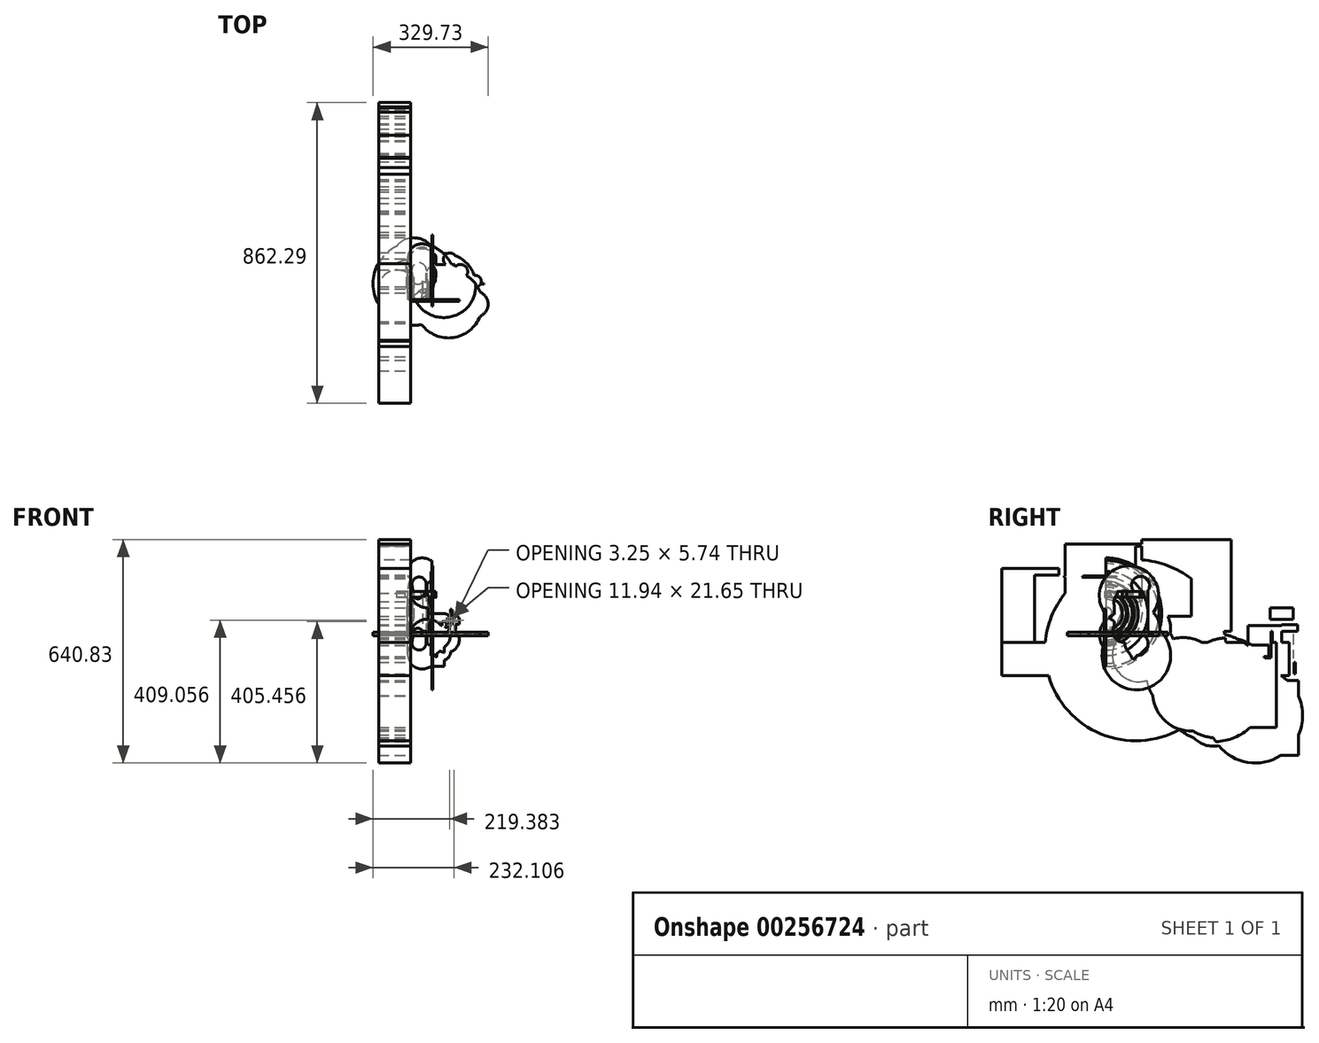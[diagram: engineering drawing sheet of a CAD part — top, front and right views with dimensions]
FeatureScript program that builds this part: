
annotation { "Feature Type Name" : "Feature", "Feature Type Description" : "" }
export const myFeature = defineFeature(function(context is Context, id is Id, definition is map)
    precondition{}
    {
        {
            var Q0;
            Q0=qCreatedBy(makeId("Top.planeOp"),FACE);
            var sketch = newSketch(context, id + "F0", { "sketchPlane" : qUnion([Q0])});
            skCircle(sketch, "E0", {"center": v(3, 0) * mm, "radius": 59.26 * mm});
            skCircle(sketch, "E1", {"center": v(60.76, 0) * mm, "radius": 10.8 * mm});
            skCircle(sketch, "E2", {"center": v(-11.73, 4.21) * mm, "radius": 51.95 * mm});
            skCircle(sketch, "E3", {"center": v(26.17, -8.72) * mm, "radius": 40 * mm});
            skCircle(sketch, "E4", {"center": v(-2.7, 22.56) * mm, "radius": 6.86 * mm});
            skCircle(sketch, "E5", {"center": v(9.93, 33.09) * mm, "radius": 17.65 * mm});
            skCircle(sketch, "E6", {"center": v(29.48, 15.94) * mm, "radius": 43.32 * mm});
            skCircle(sketch, "E7", {"center": v(-30.68, -24.97) * mm, "radius": 24.63 * mm});
            skCircle(sketch, "E8", {"center": v(16.24, 43.01) * mm, "radius": 6.92 * mm});
            skLineSegment(sketch, "E9.bottom", {"start": v(-9.54, 34.78) * mm, "end": v(37.9, 34.78) * mm});
            skLineSegment(sketch, "E9.top", {"start": v(-9.54, 34.9) * mm, "end": v(37.9, 34.9) * mm});
            skLineSegment(sketch, "E9.left", {"start": v(-9.54, 34.78) * mm, "end": v(-9.54, 34.9) * mm});
            skLineSegment(sketch, "E9.right", {"start": v(37.9, 34.78) * mm, "end": v(37.9, 34.9) * mm});
            skLineSegment(sketch, "E10.bottom", {"start": v(-6.92, -8.42) * mm, "end": v(-20.75, -8.42) * mm});
            skLineSegment(sketch, "E10.top", {"start": v(-6.92, -25.87) * mm, "end": v(-20.75, -25.87) * mm});
            skLineSegment(sketch, "E10.left", {"start": v(-6.92, -8.42) * mm, "end": v(-6.92, -25.87) * mm});
            skLineSegment(sketch, "E10.right", {"start": v(-20.75, -8.42) * mm, "end": v(-20.75, -25.87) * mm});
            skLineSegment(sketch, "E11.bottom", {"start": v(-21.06, -25.87) * mm, "end": v(-3.3, -25.87) * mm});
            skLineSegment(sketch, "E11.top", {"start": v(-21.06, -8.12) * mm, "end": v(-3.3, -8.12) * mm});
            skLineSegment(sketch, "E11.left", {"start": v(-21.06, -25.87) * mm, "end": v(-21.06, -8.12) * mm});
            skLineSegment(sketch, "E11.right", {"start": v(-3.3, -25.87) * mm, "end": v(-3.3, -8.12) * mm});
            skLineSegment(sketch, "E12.bottom", {"start": v(6.32, 9.93) * mm, "end": v(6.92, 9.93) * mm});
            skLineSegment(sketch, "E12.top", {"start": v(6.32, 15.64) * mm, "end": v(6.92, 15.64) * mm});
            skLineSegment(sketch, "E12.left", {"start": v(6.32, 9.93) * mm, "end": v(6.32, 15.64) * mm});
            skLineSegment(sketch, "E12.right", {"start": v(6.92, 9.93) * mm, "end": v(6.92, 15.64) * mm});
            skLineSegment(sketch, "E13.bottom", {"start": v(-0.9, -17.75) * mm, "end": v(-3, -17.75) * mm});
            skLineSegment(sketch, "E13.top", {"start": v(-0.9, -37.3) * mm, "end": v(-3, -37.3) * mm});
            skLineSegment(sketch, "E13.left", {"start": v(-0.9, -17.75) * mm, "end": v(-0.9, -37.3) * mm});
            skLineSegment(sketch, "E13.right", {"start": v(-3, -17.75) * mm, "end": v(-3, -37.3) * mm});
            skLineSegment(sketch, "E14.bottom", {"start": v(-0.9, -37.3) * mm, "end": v(18.05, -37.3) * mm});
            skLineSegment(sketch, "E14.top", {"start": v(-0.9, -31.58) * mm, "end": v(18.05, -31.58) * mm});
            skLineSegment(sketch, "E14.left", {"start": v(-0.9, -37.3) * mm, "end": v(-0.9, -31.58) * mm});
            skLineSegment(sketch, "E14.right", {"start": v(18.05, -37.3) * mm, "end": v(18.05, -31.58) * mm});
            skLineSegment(sketch, "E15.bottom", {"start": v(23.46, -22.56) * mm, "end": v(18.05, -22.56) * mm});
            skLineSegment(sketch, "E15.top", {"start": v(23.46, -1.5) * mm, "end": v(18.05, -1.5) * mm});
            skLineSegment(sketch, "E15.left", {"start": v(23.46, -22.56) * mm, "end": v(23.46, -1.5) * mm});
            skLineSegment(sketch, "E15.right", {"start": v(18.05, -22.56) * mm, "end": v(18.05, -1.5) * mm});
            skLineSegment(sketch, "E16.bottom", {"start": v(16.84, -0.3) * mm, "end": v(63.77, -0.3) * mm});
            skLineSegment(sketch, "E16.top", {"start": v(16.84, 50.23) * mm, "end": v(63.77, 50.23) * mm});
            skLineSegment(sketch, "E16.left", {"start": v(16.84, -0.3) * mm, "end": v(16.84, 50.23) * mm});
            skLineSegment(sketch, "E16.right", {"start": v(63.77, -0.3) * mm, "end": v(63.77, 50.23) * mm});
            skLineSegment(sketch, "E17.bottom", {"start": v(35.14, -27) * mm, "end": v(-31.88, -27) * mm});
            skLineSegment(sketch, "E17.top", {"start": v(35.14, 42.71) * mm, "end": v(-31.88, 42.71) * mm});
            skLineSegment(sketch, "E17.left", {"start": v(35.14, -27) * mm, "end": v(35.14, 42.71) * mm});
            skLineSegment(sketch, "E17.right", {"start": v(-31.88, -27) * mm, "end": v(-31.88, 42.71) * mm});
            skSolve(sketch);
        }
        {
            var Q0;
            Q0 = qSketchRegion(id + "F0", true);
            extrude(context, id + "F1", {"entities" : qUnion([Q0]), "depth" : 17.53 * mm});
        }
        {
            var Q0;
            {var subQ0=sQuery(id+"F0.wireOp",EDGE,"E16.right");Q0=makeQuery(id+"F1.opExtrude","SWEPT_FACE",FACE,{"disambiguationData":[OSD([subQ0]),TDD([makeQuery(id+"F0.imprint","IMPRINT",EDGE,{"disambiguationData":[TD([[makeQuery(id+"F0.imprint","INTERSECT",VERTEX,{"derivedFrom":[sQuery(id+"F0.wireOp",EDGE,"E1"),subQ0]}),1.0]])],"derivedFrom":subQ0})])]});}
            var sketch = newSketch(context, id + "F2", { "sketchPlane" : qUnion([Q0])});
            skCircle(sketch, "E18", {"center": v(-10.37, 5.14) * mm, "radius": 85.17 * mm});
            skCircle(sketch, "E19", {"center": v(-43.61, 34.5) * mm, "radius": 25.84 * mm});
            skCircle(sketch, "E20", {"center": v(-26.77, -16.98) * mm, "radius": 29.62 * mm});
            skCircle(sketch, "E21", {"center": v(0.3, -14.85) * mm, "radius": 32.69 * mm});
            skCircle(sketch, "E22", {"center": v(3.91, -97.37) * mm, "radius": 31.8 * mm});
            skCircle(sketch, "E23", {"center": v(-25.27, -65.04) * mm, "radius": 7.85 * mm});
            skCircle(sketch, "E24", {"center": v(-34.3, -47.6) * mm, "radius": 19.67 * mm});
            skCircle(sketch, "E25", {"center": v(-24.06, -169.26) * mm, "radius": 7.04 * mm});
            skCircle(sketch, "E26", {"center": v(-32.79, -122.47) * mm, "radius": 16.44 * mm});
            skCircle(sketch, "E27", {"center": v(-41.8, -88.01) * mm, "radius": 57.72 * mm});
            skCircle(sketch, "E28", {"center": v(11.43, -107.58) * mm, "radius": 62.26 * mm});
            skCircle(sketch, "E29", {"center": v(-19.55, -161.18) * mm, "radius": 6.63 * mm});
            skCircle(sketch, "E30", {"center": v(-32.18, -133.53) * mm, "radius": 33.19 * mm});
            skCircle(sketch, "E31", {"center": v(-31.58, -166.7) * mm, "radius": 98.41 * mm});
            skLineSegment(sketch, "E32.bottom", {"start": v(0, -65.82) * mm, "end": v(12.03, -65.82) * mm});
            skLineSegment(sketch, "E32.top", {"start": v(0, -38.67) * mm, "end": v(12.03, -38.67) * mm});
            skLineSegment(sketch, "E32.left", {"start": v(0, -65.82) * mm, "end": v(0, -38.67) * mm});
            skLineSegment(sketch, "E32.right", {"start": v(12.03, -65.82) * mm, "end": v(12.03, -38.67) * mm});
            skLineSegment(sketch, "E33.bottom", {"start": v(18.05, -31.86) * mm, "end": v(-13.18, -31.86) * mm});
            skLineSegment(sketch, "E33.top", {"start": v(18.05, -124.18) * mm, "end": v(-13.18, -124.18) * mm});
            skLineSegment(sketch, "E33.left", {"start": v(18.05, -31.86) * mm, "end": v(18.05, -124.18) * mm});
            skLineSegment(sketch, "E33.right", {"start": v(-13.18, -31.86) * mm, "end": v(-13.18, -124.18) * mm});
            skLineSegment(sketch, "E34.bottom", {"start": v(-8.12, -118.22) * mm, "end": v(-37.9, -118.22) * mm});
            skLineSegment(sketch, "E34.top", {"start": v(-8.12, -5.92) * mm, "end": v(-37.9, -5.92) * mm});
            skLineSegment(sketch, "E34.left", {"start": v(-8.12, -118.22) * mm, "end": v(-8.12, -5.92) * mm});
            skLineSegment(sketch, "E34.right", {"start": v(-37.9, -118.22) * mm, "end": v(-37.9, -5.92) * mm});
            skLineSegment(sketch, "E35.bottom", {"start": v(32.3, -8.23) * mm, "end": v(-46.92, -8.23) * mm});
            skLineSegment(sketch, "E35.top", {"start": v(32.3, -108.86) * mm, "end": v(-46.92, -108.86) * mm});
            skLineSegment(sketch, "E35.left", {"start": v(32.3, -8.23) * mm, "end": v(32.3, -108.86) * mm});
            skLineSegment(sketch, "E35.right", {"start": v(-46.92, -8.23) * mm, "end": v(-46.92, -108.86) * mm});
            skLineSegment(sketch, "E36.bottom", {"start": v(-64.67, -110.13) * mm, "end": v(61.36, -110.13) * mm});
            skLineSegment(sketch, "E36.top", {"start": v(-64.67, 41.3) * mm, "end": v(61.36, 41.3) * mm});
            skLineSegment(sketch, "E36.left", {"start": v(-64.67, -110.13) * mm, "end": v(-64.67, 41.3) * mm});
            skLineSegment(sketch, "E36.right", {"start": v(61.36, -110.13) * mm, "end": v(61.36, 41.3) * mm});
            skSolve(sketch);
        }
        {
            var Q0;
            Q0 = qSketchRegion(id + "F2", true);
            extrude(context, id + "F3", {"entities" : qUnion([Q0]), "operationType" : NewBodyOperationType.ADD, "depth" : 2.54 * mm});
        }
        {
            var Q0;
            {var subQ0=sQuery(id+"F2.wireOp",EDGE,"E36.bottom");Q0=makeQuery(id+"F3.opExtrude","SWEPT_FACE",FACE,{"disambiguationData":[OSD([subQ0]),TDD([makeQuery(id+"F2.imprint","IMPRINT",EDGE,{"disambiguationData":[TD([[makeQuery(id+"F2.imprint","INTERSECT",VERTEX,{"derivedFrom":[subQ0,sQuery(id+"F2.wireOp",EDGE,"E36.left")]}),-1.0]])],"derivedFrom":subQ0})])]});}
            var sketch = newSketch(context, id + "F4", { "sketchPlane" : qUnion([Q0])});
            skLineSegment(sketch, "E37.bottom", {"start": v(32.71, 16.54) * mm, "end": v(45.9, 16.54) * mm});
            skLineSegment(sketch, "E37.top", {"start": v(32.71, 11.73) * mm, "end": v(45.9, 11.73) * mm});
            skLineSegment(sketch, "E37.left", {"start": v(32.71, 16.54) * mm, "end": v(32.71, 11.73) * mm});
            skLineSegment(sketch, "E37.right", {"start": v(45.9, 16.54) * mm, "end": v(45.9, 11.73) * mm});
            skLineSegment(sketch, "E38.bottom", {"start": v(97.8, -17.45) * mm, "end": v(125.87, -17.45) * mm});
            skLineSegment(sketch, "E38.top", {"start": v(97.8, -33.39) * mm, "end": v(125.87, -33.39) * mm});
            skLineSegment(sketch, "E38.left", {"start": v(97.8, -17.45) * mm, "end": v(97.8, -33.39) * mm});
            skLineSegment(sketch, "E38.right", {"start": v(125.87, -17.45) * mm, "end": v(125.87, -33.39) * mm});
            skLineSegment(sketch, "E39.bottom", {"start": v(127.57, -33.39) * mm, "end": v(4.64, -33.39) * mm});
            skLineSegment(sketch, "E39.top", {"start": v(127.57, 44.52) * mm, "end": v(4.64, 44.52) * mm});
            skLineSegment(sketch, "E39.left", {"start": v(127.57, -33.39) * mm, "end": v(127.57, 44.52) * mm});
            skLineSegment(sketch, "E39.right", {"start": v(4.64, -33.39) * mm, "end": v(4.64, 44.52) * mm});
            skLineSegment(sketch, "E40.bottom", {"start": v(4.64, 44.52) * mm, "end": v(125.87, 44.52) * mm});
            skLineSegment(sketch, "E40.top", {"start": v(4.64, -21.06) * mm, "end": v(125.87, -21.06) * mm});
            skLineSegment(sketch, "E40.left", {"start": v(4.64, 44.52) * mm, "end": v(4.64, -21.06) * mm});
            skLineSegment(sketch, "E40.right", {"start": v(125.87, 44.52) * mm, "end": v(125.87, -21.06) * mm});
            skLineSegment(sketch, "E41.bottom", {"start": v(199.04, -10.83) * mm, "end": v(211.37, -10.83) * mm});
            skLineSegment(sketch, "E41.top", {"start": v(199.04, -9.93) * mm, "end": v(211.37, -9.93) * mm});
            skLineSegment(sketch, "E41.left", {"start": v(199.04, -10.83) * mm, "end": v(199.04, -9.93) * mm});
            skLineSegment(sketch, "E41.right", {"start": v(211.37, -10.83) * mm, "end": v(211.37, -9.93) * mm});
            skLineSegment(sketch, "E42.bottom", {"start": v(213.08, -9.93) * mm, "end": v(61.22, -9.93) * mm});
            skLineSegment(sketch, "E42.top", {"start": v(213.08, -9.93) * mm, "end": v(61.22, -9.93) * mm});
            skLineSegment(sketch, "E42.left", {"start": v(213.08, -9.93) * mm, "end": v(213.08, -9.93) * mm});
            skLineSegment(sketch, "E42.right", {"start": v(61.22, -9.93) * mm, "end": v(61.22, -9.93) * mm});
            skLineSegment(sketch, "E43.bottom", {"start": v(61.22, -8.72) * mm, "end": v(68.02, -8.72) * mm});
            skLineSegment(sketch, "E43.top", {"start": v(61.22, 2.7) * mm, "end": v(68.02, 2.7) * mm});
            skLineSegment(sketch, "E43.left", {"start": v(61.22, -8.72) * mm, "end": v(61.22, 2.7) * mm});
            skLineSegment(sketch, "E43.right", {"start": v(68.02, -8.72) * mm, "end": v(68.02, 2.7) * mm});
            skLineSegment(sketch, "E44.bottom", {"start": v(92.7, 24.97) * mm, "end": v(112.26, 24.97) * mm});
            skLineSegment(sketch, "E44.top", {"start": v(92.7, 36.1) * mm, "end": v(112.26, 36.1) * mm});
            skLineSegment(sketch, "E44.left", {"start": v(92.7, 24.97) * mm, "end": v(92.7, 36.1) * mm});
            skLineSegment(sketch, "E44.right", {"start": v(112.26, 24.97) * mm, "end": v(112.26, 36.1) * mm});
            skLineSegment(sketch, "E45.bottom", {"start": v(123.75, 38.5) * mm, "end": v(65.04, 38.5) * mm});
            skLineSegment(sketch, "E45.top", {"start": v(123.75, -46.92) * mm, "end": v(65.04, -46.92) * mm});
            skLineSegment(sketch, "E45.left", {"start": v(123.75, 38.5) * mm, "end": v(123.75, -46.92) * mm});
            skLineSegment(sketch, "E45.right", {"start": v(65.04, 38.5) * mm, "end": v(65.04, -46.92) * mm});
            skLineSegment(sketch, "E46.bottom", {"start": v(65.04, -46.92) * mm, "end": v(7.2, -46.92) * mm});
            skLineSegment(sketch, "E46.top", {"start": v(65.04, -56.25) * mm, "end": v(7.2, -56.25) * mm});
            skLineSegment(sketch, "E46.left", {"start": v(65.04, -46.92) * mm, "end": v(65.04, -56.25) * mm});
            skLineSegment(sketch, "E46.right", {"start": v(7.2, -46.92) * mm, "end": v(7.2, -56.25) * mm});
            skLineSegment(sketch, "E47.bottom", {"start": v(-51.94, -60.46) * mm, "end": v(83.76, -60.46) * mm});
            skLineSegment(sketch, "E47.top", {"start": v(-51.94, -50.53) * mm, "end": v(83.76, -50.53) * mm});
            skLineSegment(sketch, "E47.left", {"start": v(-51.94, -60.46) * mm, "end": v(-51.94, -50.53) * mm});
            skLineSegment(sketch, "E47.right", {"start": v(83.76, -60.46) * mm, "end": v(83.76, -50.53) * mm});
            skLineSegment(sketch, "E48.bottom", {"start": v(113.11, -52.04) * mm, "end": v(126.3, -52.04) * mm});
            skLineSegment(sketch, "E48.top", {"start": v(113.11, -53.54) * mm, "end": v(126.3, -53.54) * mm});
            skLineSegment(sketch, "E48.left", {"start": v(113.11, -52.04) * mm, "end": v(113.11, -53.54) * mm});
            skLineSegment(sketch, "E48.right", {"start": v(126.3, -52.04) * mm, "end": v(126.3, -53.54) * mm});
            skLineSegment(sketch, "E49.bottom", {"start": v(140.76, -44.22) * mm, "end": v(153.52, -44.22) * mm});
            skLineSegment(sketch, "E49.top", {"start": v(140.76, -36.7) * mm, "end": v(153.52, -36.7) * mm});
            skLineSegment(sketch, "E49.left", {"start": v(140.76, -44.22) * mm, "end": v(140.76, -36.7) * mm});
            skLineSegment(sketch, "E49.right", {"start": v(153.52, -44.22) * mm, "end": v(153.52, -36.7) * mm});
            skLineSegment(sketch, "E50.bottom", {"start": v(130.98, -11.43) * mm, "end": v(102.9, -11.43) * mm});
            skLineSegment(sketch, "E50.top", {"start": v(130.98, -6.02) * mm, "end": v(102.9, -6.02) * mm});
            skLineSegment(sketch, "E50.left", {"start": v(130.98, -11.43) * mm, "end": v(130.98, -6.02) * mm});
            skLineSegment(sketch, "E50.right", {"start": v(102.9, -11.43) * mm, "end": v(102.9, -6.02) * mm});
            skLineSegment(sketch, "E51.bottom", {"start": v(28.04, -4.51) * mm, "end": v(-6.42, -4.51) * mm});
            skLineSegment(sketch, "E51.top", {"start": v(28.04, -0.6) * mm, "end": v(-6.42, -0.6) * mm});
            skLineSegment(sketch, "E51.left", {"start": v(28.04, -4.51) * mm, "end": v(28.04, -0.6) * mm});
            skLineSegment(sketch, "E51.right", {"start": v(-6.42, -4.51) * mm, "end": v(-6.42, -0.6) * mm});
            skLineSegment(sketch, "E52.bottom", {"start": v(5.06, 20.45) * mm, "end": v(11.87, 20.45) * mm});
            skLineSegment(sketch, "E52.top", {"start": v(5.06, 24.66) * mm, "end": v(11.87, 24.66) * mm});
            skLineSegment(sketch, "E52.left", {"start": v(5.06, 20.45) * mm, "end": v(5.06, 24.66) * mm});
            skLineSegment(sketch, "E52.right", {"start": v(11.87, 20.45) * mm, "end": v(11.87, 24.66) * mm});
            skLineSegment(sketch, "E53.bottom", {"start": v(31.44, 30.08) * mm, "end": v(84.61, 30.08) * mm});
            skLineSegment(sketch, "E53.top", {"start": v(31.44, 37.9) * mm, "end": v(84.61, 37.9) * mm});
            skLineSegment(sketch, "E53.left", {"start": v(31.44, 30.08) * mm, "end": v(31.44, 37.9) * mm});
            skLineSegment(sketch, "E53.right", {"start": v(84.61, 30.08) * mm, "end": v(84.61, 37.9) * mm});
            skLineSegment(sketch, "E54.bottom", {"start": v(111.4, 28.88) * mm, "end": v(118.22, 28.88) * mm});
            skLineSegment(sketch, "E54.top", {"start": v(111.4, -59.26) * mm, "end": v(118.22, -59.26) * mm});
            skLineSegment(sketch, "E54.left", {"start": v(111.4, 28.88) * mm, "end": v(111.4, -59.26) * mm});
            skLineSegment(sketch, "E54.right", {"start": v(118.22, 28.88) * mm, "end": v(118.22, -59.26) * mm});
            skLineSegment(sketch, "E55.bottom", {"start": v(106.73, -64.07) * mm, "end": v(100.78, -64.07) * mm});
            skLineSegment(sketch, "E55.top", {"start": v(106.73, -65.87) * mm, "end": v(100.78, -65.87) * mm});
            skLineSegment(sketch, "E55.left", {"start": v(106.73, -64.07) * mm, "end": v(106.73, -65.87) * mm});
            skLineSegment(sketch, "E55.right", {"start": v(100.78, -64.07) * mm, "end": v(100.78, -65.87) * mm});
            skCircle(sketch, "E56", {"center": v(-17.9, 5.41) * mm, "radius": 11.2 * mm});
            skCircle(sketch, "E57", {"center": v(-6.85, 3.6) * mm, "radius": 19.8 * mm});
            skCircle(sketch, "E58", {"center": v(185, -69.18) * mm, "radius": 37.42 * mm});
            skCircle(sketch, "E59", {"center": v(128.85, -46.02) * mm, "radius": 47.67 * mm});
            skCircle(sketch, "E60", {"center": v(81.2, -43.92) * mm, "radius": 30.92 * mm});
            skCircle(sketch, "E61", {"center": v(108.86, -68.88) * mm, "radius": 96.95 * mm});
            skCircle(sketch, "E62", {"center": v(15.7, 38.8) * mm, "radius": 29.27 * mm});
            skCircle(sketch, "E63", {"center": v(9.74, 58.05) * mm, "radius": 63.19 * mm});
            skCircle(sketch, "E64", {"center": v(113.11, 58.65) * mm, "radius": 18.97 * mm});
            skCircle(sketch, "E65", {"center": v(143.31, 24.06) * mm, "radius": 20.76 * mm});
            skCircle(sketch, "E66", {"center": v(-38.75, -23.76) * mm, "radius": 52.4 * mm});
            skCircle(sketch, "E67", {"center": v(11.87, -10.23) * mm, "radius": 119.18 * mm});
            skCircle(sketch, "E68", {"center": v(133.1, -9.32) * mm, "radius": 12.68 * mm});
            skCircle(sketch, "E69", {"center": v(95.25, -15.64) * mm, "radius": 91.99 * mm});
            skCircle(sketch, "E70", {"center": v(186.28, -3.3) * mm, "radius": 16.6 * mm});
            skSolve(sketch);
        }
        {
            var Q0;
            Q0 = qSketchRegion(id + "F4", true);
            extrude(context, id + "F5", {"entities" : qUnion([Q0]), "operationType" : NewBodyOperationType.ADD, "depth" : 10.67 * mm});
        }
        {
            var Q0;
            Q0=makeQuery(id+"F5.opExtrude","SWEPT_FACE",FACE,{"disambiguationData":[OSD([sQuery(id+"F4.wireOp",EDGE,"E47.bottom")])]});
            var sketch = newSketch(context, id + "F6", { "sketchPlane" : qUnion([Q0])});
            skCircle(sketch, "E71", {"center": v(-48.59, -115.37) * mm, "radius": 52.6 * mm});
            skCircle(sketch, "E72", {"center": v(-33.23, -163.82) * mm, "radius": 41.84 * mm});
            skCircle(sketch, "E73", {"center": v(-26.98, -120.14) * mm, "radius": 21.12 * mm});
            skCircle(sketch, "E74", {"center": v(-39.9, -105.41) * mm, "radius": 8.6 * mm});
            skCircle(sketch, "E75", {"center": v(-21.12, -101.94) * mm, "radius": 13.58 * mm});
            skCircle(sketch, "E76", {"center": v(4.89, -108.69) * mm, "radius": 6.25 * mm});
            skCircle(sketch, "E77", {"center": v(-3, -121.26) * mm, "radius": 11.8 * mm});
            skCircle(sketch, "E78", {"center": v(-24.5, -130.43) * mm, "radius": 20.57 * mm});
            skCircle(sketch, "E79", {"center": v(-61.33, -124.29) * mm, "radius": 14.83 * mm});
            skCircle(sketch, "E80", {"center": v(-80.55, -112.88) * mm, "radius": 33.17 * mm});
            skCircle(sketch, "E81", {"center": v(-91.4, -84.6) * mm, "radius": 38.52 * mm});
            skCircle(sketch, "E82", {"center": v(-102.7, -121.42) * mm, "radius": 36.94 * mm});
            skCircle(sketch, "E83", {"center": v(-91.55, -156.63) * mm, "radius": 23.58 * mm});
            skLineSegment(sketch, "E84.bottom", {"start": v(-96.93, -198.17) * mm, "end": v(-58.06, -198.17) * mm});
            skLineSegment(sketch, "E84.top", {"start": v(-96.93, -88.5) * mm, "end": v(-58.06, -88.5) * mm});
            skLineSegment(sketch, "E84.left", {"start": v(-96.93, -198.17) * mm, "end": v(-96.93, -88.5) * mm});
            skLineSegment(sketch, "E84.right", {"start": v(-58.06, -198.17) * mm, "end": v(-58.06, -88.5) * mm});
            skLineSegment(sketch, "E85.bottom", {"start": v(-60.99, -90.34) * mm, "end": v(-68.2, -90.34) * mm});
            skLineSegment(sketch, "E85.top", {"start": v(-60.99, -94.57) * mm, "end": v(-68.2, -94.57) * mm});
            skLineSegment(sketch, "E85.left", {"start": v(-60.99, -90.34) * mm, "end": v(-60.99, -94.57) * mm});
            skLineSegment(sketch, "E85.right", {"start": v(-68.2, -90.34) * mm, "end": v(-68.2, -94.57) * mm});
            skLineSegment(sketch, "E86.bottom", {"start": v(-83.7, -93.49) * mm, "end": v(-112.61, -93.49) * mm});
            skLineSegment(sketch, "E86.top", {"start": v(-83.7, -86.24) * mm, "end": v(-112.61, -86.24) * mm});
            skLineSegment(sketch, "E86.left", {"start": v(-83.7, -93.49) * mm, "end": v(-83.7, -86.24) * mm});
            skLineSegment(sketch, "E86.right", {"start": v(-112.61, -93.49) * mm, "end": v(-112.61, -86.24) * mm});
            skLineSegment(sketch, "E87.bottom", {"start": v(-135.42, -72.46) * mm, "end": v(-129.16, -72.46) * mm});
            skLineSegment(sketch, "E87.top", {"start": v(-135.42, -53.45) * mm, "end": v(-129.16, -53.45) * mm});
            skLineSegment(sketch, "E87.left", {"start": v(-135.42, -72.46) * mm, "end": v(-135.42, -53.45) * mm});
            skLineSegment(sketch, "E87.right", {"start": v(-129.16, -72.46) * mm, "end": v(-129.16, -53.45) * mm});
            skLineSegment(sketch, "E88.bottom", {"start": v(-121.8, -51.19) * mm, "end": v(-114.29, -51.19) * mm});
            skLineSegment(sketch, "E88.top", {"start": v(-121.8, -53.88) * mm, "end": v(-114.29, -53.88) * mm});
            skLineSegment(sketch, "E88.left", {"start": v(-121.8, -51.19) * mm, "end": v(-121.8, -53.88) * mm});
            skLineSegment(sketch, "E88.right", {"start": v(-114.29, -51.19) * mm, "end": v(-114.29, -53.88) * mm});
            skLineSegment(sketch, "E89.bottom", {"start": v(-102.9, -68.88) * mm, "end": v(-89.86, -68.88) * mm});
            skLineSegment(sketch, "E89.top", {"start": v(-102.9, -84.33) * mm, "end": v(-89.86, -84.33) * mm});
            skLineSegment(sketch, "E89.left", {"start": v(-102.9, -68.88) * mm, "end": v(-102.9, -84.33) * mm});
            skLineSegment(sketch, "E89.right", {"start": v(-89.86, -68.88) * mm, "end": v(-89.86, -84.33) * mm});
            skLineSegment(sketch, "E90.bottom", {"start": v(-77.22, -96.36) * mm, "end": v(-62.89, -96.36) * mm});
            skLineSegment(sketch, "E90.top", {"start": v(-77.22, -102.88) * mm, "end": v(-62.89, -102.88) * mm});
            skLineSegment(sketch, "E90.left", {"start": v(-77.22, -96.36) * mm, "end": v(-77.22, -102.88) * mm});
            skLineSegment(sketch, "E90.right", {"start": v(-62.89, -96.36) * mm, "end": v(-62.89, -102.88) * mm});
            skLineSegment(sketch, "E91.bottom", {"start": v(-51.23, -106.1) * mm, "end": v(-87.55, -106.1) * mm});
            skLineSegment(sketch, "E91.top", {"start": v(-51.23, -46.27) * mm, "end": v(-87.55, -46.27) * mm});
            skLineSegment(sketch, "E91.left", {"start": v(-51.23, -106.1) * mm, "end": v(-51.23, -46.27) * mm});
            skLineSegment(sketch, "E91.right", {"start": v(-87.55, -106.1) * mm, "end": v(-87.55, -46.27) * mm});
            skLineSegment(sketch, "E92.bottom", {"start": v(-123.17, -43.2) * mm, "end": v(-126.42, -43.2) * mm});
            skLineSegment(sketch, "E92.top", {"start": v(-123.17, -68.56) * mm, "end": v(-126.42, -68.56) * mm});
            skLineSegment(sketch, "E92.left", {"start": v(-123.17, -43.2) * mm, "end": v(-123.17, -68.56) * mm});
            skLineSegment(sketch, "E92.right", {"start": v(-126.42, -43.2) * mm, "end": v(-126.42, -68.56) * mm});
            skPoint(sketch, "E93.firstSnap0", {"position": v(-89.86, -76.6) * mm});
            skLineSegment(sketch, "E93.bottom", {"start": v(-140.02, -76.6) * mm, "end": v(-106.1, -76.6) * mm});
            skLineSegment(sketch, "E93.top", {"start": v(-140.02, -58.46) * mm, "end": v(-106.1, -58.46) * mm});
            skLineSegment(sketch, "E93.left", {"start": v(-140.02, -76.6) * mm, "end": v(-140.02, -58.46) * mm});
            skLineSegment(sketch, "E93.right", {"start": v(-106.1, -76.6) * mm, "end": v(-106.1, -58.46) * mm});
            skLineSegment(sketch, "E94.bottom", {"start": v(-114.29, -43.53) * mm, "end": v(-114.29, -43.53) * mm});
            skLineSegment(sketch, "E94.top", {"start": v(-114.29, -66.7) * mm, "end": v(-114.29, -66.7) * mm});
            skLineSegment(sketch, "E94.left", {"start": v(-114.29, -43.53) * mm, "end": v(-114.29, -66.7) * mm});
            skLineSegment(sketch, "E94.right", {"start": v(-114.29, -43.53) * mm, "end": v(-114.29, -66.7) * mm});
            skPoint(sketch, "E95.oppositeSnap0", {"position": v(-118.04, -51.19) * mm});
            skLineSegment(sketch, "E95.bottom", {"start": v(-114.29, -33.62) * mm, "end": v(-118.04, -33.62) * mm});
            skLineSegment(sketch, "E95.top", {"start": v(-114.29, -80.1) * mm, "end": v(-118.04, -80.1) * mm});
            skLineSegment(sketch, "E95.left", {"start": v(-114.29, -33.62) * mm, "end": v(-114.29, -80.1) * mm});
            skLineSegment(sketch, "E95.right", {"start": v(-118.04, -33.62) * mm, "end": v(-118.04, -80.1) * mm});
            skSolve(sketch);
        }
        {
            var Q0;
            Q0 = qSketchRegion(id + "F6", true);
            extrude(context, id + "F7", {"entities" : qUnion([Q0]), "operationType" : NewBodyOperationType.ADD, "depth" : 5.08 * mm});
        }
        {
            var Q0;
            {var subQ0=sQuery(id+"F6.wireOp",EDGE,"E84.right");var subQ1=sQuery(id+"F6.wireOp",EDGE,"E71");var subQ3=sQuery(id+"F6.wireOp",EDGE,"E79");var subQ4=sQuery(id+"F6.wireOp",EDGE,"E84.bottom");var subQ5=sQuery(id+"F6.wireOp",EDGE,"E72");var subQ7=sQuery(id+"F6.wireOp",EDGE,"E81");var subQ9=sQuery(id+"F6.wireOp",EDGE,"E80");var subQ12=sQuery(id+"F6.wireOp",EDGE,"E76");var subQ14=sQuery(id+"F6.wireOp",EDGE,"E77");var subQ16=sQuery(id+"F6.wireOp",EDGE,"E91.left");var subQ18=sQuery(id+"F6.wireOp",EDGE,"E74");var subQ23=sQuery(id+"F6.wireOp",EDGE,"E75");var subQ26=sQuery(id+"F6.wireOp",EDGE,"E83");var subQ28=sQuery(id+"F6.wireOp",EDGE,"E73");var subQ29=sQuery(id+"F6.wireOp",EDGE,"E78");var subQ30=sQuery(id+"F6.wireOp",EDGE,"E91.top");Q0=makeQuery(id+"F7.boolean.opBoolean","SPLIT",FACE,{"disambiguationData":[TD([makeQuery(id+"F7.opExtrude","SWEPT_FACE",FACE,{"disambiguationData":[OSD([subQ18])]})])],"derivedFrom":makeQuery(id+"F7.opExtrude","CAP_FACE",FACE,{"disambiguationData":[OSD([subQ1,subQ5,subQ28,subQ18,subQ23,subQ12,subQ14,subQ29,subQ3,subQ9,subQ7,sQuery(id+"F6.wireOp",EDGE,"E82"),subQ26,subQ4,sQuery(id+"F6.wireOp",EDGE,"E84.left"),subQ0,sQuery(id+"F6.wireOp",EDGE,"E86.bottom"),sQuery(id+"F6.wireOp",EDGE,"E86.top"),sQuery(id+"F6.wireOp",EDGE,"E86.right"),sQuery(id+"F6.wireOp",EDGE,"E87.top"),sQuery(id+"F6.wireOp",EDGE,"E87.left"),sQuery(id+"F6.wireOp",EDGE,"E87.right"),sQuery(id+"F6.wireOp",EDGE,"E88.bottom"),sQuery(id+"F6.wireOp",EDGE,"E88.top"),sQuery(id+"F6.wireOp",EDGE,"E88.left"),sQuery(id+"F6.wireOp",EDGE,"E89.bottom"),sQuery(id+"F6.wireOp",EDGE,"E89.top"),sQuery(id+"F6.wireOp",EDGE,"E89.left"),sQuery(id+"F6.wireOp",EDGE,"E89.right"),subQ30,subQ16,sQuery(id+"F6.wireOp",EDGE,"E92.bottom"),sQuery(id+"F6.wireOp",EDGE,"E92.top"),sQuery(id+"F6.wireOp",EDGE,"E92.left"),sQuery(id+"F6.wireOp",EDGE,"E92.right"),sQuery(id+"F6.wireOp",EDGE,"E93.bottom"),sQuery(id+"F6.wireOp",EDGE,"E93.top"),sQuery(id+"F6.wireOp",EDGE,"E93.left"),sQuery(id+"F6.wireOp",EDGE,"E93.right"),sQuery(id+"F6.wireOp",EDGE,"E95.bottom"),sQuery(id+"F6.wireOp",EDGE,"E95.top"),sQuery(id+"F6.wireOp",EDGE,"E95.left"),sQuery(id+"F6.wireOp",EDGE,"E95.right")])],"isStart":false})});}
            var Q1;
            {var subQ0=sQuery(id+"F6.wireOp",EDGE,"E91.left");var subQ1=sQuery(id+"F6.wireOp",EDGE,"E91.top");Q1=makeQuery(id+"F7.boolean.opBoolean","SPLIT",EDGE,{"disambiguationData":[TD([makeQuery(id+"F7.opExtrude","SWEPT_FACE",FACE,{"disambiguationData":[OSD([subQ0])]})])],"derivedFrom":makeQuery(id+"F7.opExtrude","CAP_EDGE",EDGE,{"disambiguationData":[OSD([subQ1])],"isStart":false})});}
            revolve(context, id + "F8", {"operationType" : NewBodyOperationType.ADD, "entities" : qUnion([Q0]), "axis" : qUnion([Q1]), "revolveType" : RevolveType.ONE_DIRECTION, "angle" : 180 * degree});
        }
        {
            var Q0;
            Q0=qCreatedBy(makeId("Right.planeOp"),FACE);
            var sketch = newSketch(context, id + "F9", { "sketchPlane" : qUnion([Q0])});
            skCircle(sketch, "E96", {"center": v(52.35, -89.24) * mm, "radius": 77.4 * mm});
            skCircle(sketch, "E97", {"center": v(38.12, -166.36) * mm, "radius": 75.53 * mm});
            skCircle(sketch, "E98", {"center": v(135.98, -221.45) * mm, "radius": 29.22 * mm});
            skCircle(sketch, "E99", {"center": v(66.59, -142.59) * mm, "radius": 73.83 * mm});
            skCircle(sketch, "E100", {"center": v(29.22, -151.64) * mm, "radius": 259.77 * mm});
            skCircle(sketch, "E101", {"center": v(226.72, -358.24) * mm, "radius": 28.47 * mm});
            skCircle(sketch, "E102", {"center": v(251.63, -352.2) * mm, "radius": 74.46 * mm});
            skCircle(sketch, "E103", {"center": v(187.57, -273.96) * mm, "radius": 108.82 * mm});
            skCircle(sketch, "E104", {"center": v(292.55, -245.3) * mm, "radius": 129.16 * mm});
            skCircle(sketch, "E105", {"center": v(166.22, -221.17) * mm, "radius": 106.14 * mm});
            skCircle(sketch, "E106", {"center": v(264.08, -268.04) * mm, "radius": 134.97 * mm});
            skCircle(sketch, "E107", {"center": v(372.61, -338.74) * mm, "radius": 136 * mm});
            skCircle(sketch, "E108", {"center": v(264.08, -247.5) * mm, "radius": 5.8 * mm});
            skCircle(sketch, "E109", {"center": v(264.08, -249.55) * mm, "radius": 105.85 * mm});
            skCircle(sketch, "E110", {"center": v(345.92, -305.88) * mm, "radius": 56.17 * mm});
            skCircle(sketch, "E111", {"center": v(253.4, -258.6) * mm, "radius": 155.16 * mm});
            skCircle(sketch, "E112", {"center": v(54.13, -158.96) * mm, "radius": 51.72 * mm});
            skCircle(sketch, "E113", {"center": v(146.65, -205.22) * mm, "radius": 25.25 * mm});
            skCircle(sketch, "E114", {"center": v(125.95, -170.1) * mm, "radius": 4.54 * mm});
            skCircle(sketch, "E115", {"center": v(127.08, -173.86) * mm, "radius": 43.24 * mm});
            skLineSegment(sketch, "E116.bottom", {"start": v(493.43, -77.88) * mm, "end": v(448.2, -77.88) * mm});
            skLineSegment(sketch, "E116.top", {"start": v(493.43, -97.04) * mm, "end": v(448.2, -97.04) * mm});
            skLineSegment(sketch, "E116.left", {"start": v(493.43, -77.88) * mm, "end": v(493.43, -97.04) * mm});
            skLineSegment(sketch, "E116.right", {"start": v(448.2, -77.88) * mm, "end": v(448.2, -97.04) * mm});
            skLineSegment(sketch, "E117.bottom", {"start": v(412.03, -136.39) * mm, "end": v(363.8, -136.39) * mm});
            skLineSegment(sketch, "E117.top", {"start": v(412.03, -169.7) * mm, "end": v(363.8, -169.7) * mm});
            skLineSegment(sketch, "E117.left", {"start": v(412.03, -136.39) * mm, "end": v(412.03, -169.7) * mm});
            skLineSegment(sketch, "E117.right", {"start": v(363.8, -136.39) * mm, "end": v(363.8, -169.7) * mm});
            skLineSegment(sketch, "E118.bottom", {"start": v(351.74, -174.12) * mm, "end": v(421.08, -174.12) * mm});
            skLineSegment(sketch, "E118.top", {"start": v(351.74, -97.04) * mm, "end": v(421.08, -97.04) * mm});
            skLineSegment(sketch, "E118.left", {"start": v(351.74, -174.12) * mm, "end": v(351.74, -97.04) * mm});
            skLineSegment(sketch, "E118.right", {"start": v(421.08, -174.12) * mm, "end": v(421.08, -97.04) * mm});
            skLineSegment(sketch, "E119.bottom", {"start": v(418.06, -80.23) * mm, "end": v(448.2, -80.23) * mm});
            skLineSegment(sketch, "E119.top", {"start": v(418.06, -197.99) * mm, "end": v(448.2, -197.99) * mm});
            skLineSegment(sketch, "E119.left", {"start": v(418.06, -80.23) * mm, "end": v(418.06, -197.99) * mm});
            skLineSegment(sketch, "E119.right", {"start": v(448.2, -80.23) * mm, "end": v(448.2, -197.99) * mm});
            skLineSegment(sketch, "E120.bottom", {"start": v(448.2, -238.02) * mm, "end": v(496.44, -238.02) * mm});
            skLineSegment(sketch, "E120.top", {"start": v(448.2, -453.6) * mm, "end": v(496.44, -453.6) * mm});
            skLineSegment(sketch, "E120.left", {"start": v(448.2, -238.02) * mm, "end": v(448.2, -453.6) * mm});
            skLineSegment(sketch, "E120.right", {"start": v(496.44, -238.02) * mm, "end": v(496.44, -453.6) * mm});
            skLineSegment(sketch, "E121.bottom", {"start": v(496.44, -453.6) * mm, "end": v(363.8, -453.6) * mm});
            skLineSegment(sketch, "E121.top", {"start": v(496.44, -367.62) * mm, "end": v(363.8, -367.62) * mm});
            skLineSegment(sketch, "E121.left", {"start": v(496.44, -453.6) * mm, "end": v(496.44, -367.62) * mm});
            skLineSegment(sketch, "E121.right", {"start": v(363.8, -453.6) * mm, "end": v(363.8, -367.62) * mm});
            skLineSegment(sketch, "E122.bottom", {"start": v(351.74, -372.54) * mm, "end": v(433.14, -372.54) * mm});
            skLineSegment(sketch, "E122.top", {"start": v(351.74, -80.23) * mm, "end": v(433.14, -80.23) * mm});
            skLineSegment(sketch, "E122.left", {"start": v(351.74, -372.54) * mm, "end": v(351.74, -80.23) * mm});
            skLineSegment(sketch, "E122.right", {"start": v(433.14, -372.54) * mm, "end": v(433.14, -80.23) * mm});
            skLineSegment(sketch, "E123.bottom", {"start": v(415.05, -63.05) * mm, "end": v(481.37, -63.05) * mm});
            skLineSegment(sketch, "E123.top", {"start": v(415.05, -30.08) * mm, "end": v(481.37, -30.08) * mm});
            skLineSegment(sketch, "E123.left", {"start": v(415.05, -63.05) * mm, "end": v(415.05, -30.08) * mm});
            skLineSegment(sketch, "E123.right", {"start": v(481.37, -63.05) * mm, "end": v(481.37, -30.08) * mm});
            skLineSegment(sketch, "E124.bottom", {"start": v(481.37, -104.92) * mm, "end": v(481.37, -104.92) * mm});
            skLineSegment(sketch, "E124.top", {"start": v(481.37, -174.54) * mm, "end": v(481.37, -174.54) * mm});
            skLineSegment(sketch, "E124.left", {"start": v(481.37, -104.92) * mm, "end": v(481.37, -174.54) * mm});
            skLineSegment(sketch, "E124.right", {"start": v(481.37, -104.92) * mm, "end": v(481.37, -174.54) * mm});
            skLineSegment(sketch, "E125.bottom", {"start": v(484.39, -186.49) * mm, "end": v(487.4, -186.49) * mm});
            skLineSegment(sketch, "E125.top", {"start": v(484.39, -219.32) * mm, "end": v(487.4, -219.32) * mm});
            skLineSegment(sketch, "E125.left", {"start": v(484.39, -186.49) * mm, "end": v(484.39, -219.32) * mm});
            skLineSegment(sketch, "E125.right", {"start": v(487.4, -186.49) * mm, "end": v(487.4, -219.32) * mm});
            skLineSegment(sketch, "E126.bottom", {"start": v(469.31, -224.2) * mm, "end": v(-353.68, -224.2) * mm});
            skLineSegment(sketch, "E126.top", {"start": v(469.31, -129.48) * mm, "end": v(-353.68, -129.48) * mm});
            skLineSegment(sketch, "E126.left", {"start": v(469.31, -224.2) * mm, "end": v(469.31, -129.48) * mm});
            skLineSegment(sketch, "E126.right", {"start": v(-353.68, -224.2) * mm, "end": v(-353.68, -129.48) * mm});
            skLineSegment(sketch, "E127.bottom", {"start": v(-353.68, -129.48) * mm, "end": v(-260.23, -129.48) * mm});
            skLineSegment(sketch, "E127.top", {"start": v(-353.68, 83.13) * mm, "end": v(-260.23, 83.13) * mm});
            skLineSegment(sketch, "E127.left", {"start": v(-353.68, -129.48) * mm, "end": v(-353.68, 83.13) * mm});
            skLineSegment(sketch, "E127.right", {"start": v(-260.23, -129.48) * mm, "end": v(-260.23, 83.13) * mm});
            skLineSegment(sketch, "E128.bottom", {"start": v(-260.23, 83.13) * mm, "end": v(-190.9, 83.13) * mm});
            skLineSegment(sketch, "E128.top", {"start": v(-260.23, 64.13) * mm, "end": v(-190.9, 64.13) * mm});
            skLineSegment(sketch, "E128.left", {"start": v(-260.23, 83.13) * mm, "end": v(-260.23, 64.13) * mm});
            skLineSegment(sketch, "E128.right", {"start": v(-190.9, 83.13) * mm, "end": v(-190.9, 64.13) * mm});
            skLineSegment(sketch, "E129.bottom", {"start": v(-175.82, 61.81) * mm, "end": v(-25.09, 61.81) * mm});
            skLineSegment(sketch, "E129.top", {"start": v(-175.82, 57.8) * mm, "end": v(-25.09, 57.8) * mm});
            skLineSegment(sketch, "E129.left", {"start": v(-175.82, 61.81) * mm, "end": v(-175.82, 57.8) * mm});
            skLineSegment(sketch, "E129.right", {"start": v(-25.09, 61.81) * mm, "end": v(-25.09, 57.8) * mm});
            skLineSegment(sketch, "E130.bottom", {"start": v(29.18, 81.15) * mm, "end": v(47.26, 81.15) * mm});
            skLineSegment(sketch, "E130.top", {"start": v(29.18, 146.95) * mm, "end": v(47.26, 146.95) * mm});
            skLineSegment(sketch, "E130.left", {"start": v(29.18, 81.15) * mm, "end": v(29.18, 146.95) * mm});
            skLineSegment(sketch, "E130.right", {"start": v(47.26, 81.15) * mm, "end": v(47.26, 146.95) * mm});
            skLineSegment(sketch, "E131.bottom", {"start": v(47.26, 166.1) * mm, "end": v(303.5, 166.1) * mm});
            skLineSegment(sketch, "E131.top", {"start": v(47.26, -97.04) * mm, "end": v(303.5, -97.04) * mm});
            skLineSegment(sketch, "E131.left", {"start": v(47.26, 166.1) * mm, "end": v(47.26, -97.04) * mm});
            skLineSegment(sketch, "E131.right", {"start": v(303.5, 166.1) * mm, "end": v(303.5, -97.04) * mm});
            skLineSegment(sketch, "E132.bottom", {"start": v(188.95, -54.44) * mm, "end": v(-172.8, -54.44) * mm});
            skLineSegment(sketch, "E132.top", {"start": v(188.95, 152.55) * mm, "end": v(-172.8, 152.55) * mm});
            skLineSegment(sketch, "E132.left", {"start": v(188.95, -54.44) * mm, "end": v(188.95, 152.55) * mm});
            skLineSegment(sketch, "E132.right", {"start": v(-172.8, -54.44) * mm, "end": v(-172.8, 152.55) * mm});
            skSolve(sketch);
        }
        {
            var Q0;
            Q0 = qSketchRegion(id + "F9", true);
            extrude(context, id + "F10", {"entities" : qUnion([Q0]), "operationType" : NewBodyOperationType.ADD, "oppositeDirection" : true, "depth" : 91.44 * mm});
        }
    });
